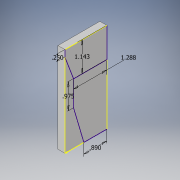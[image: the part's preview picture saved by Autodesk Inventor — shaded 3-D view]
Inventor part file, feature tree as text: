
AUTODESK INVENTOR PART (.ipt)
format: ipt  version: 2018 (Build 220112000, 112)  size: 104,448 bytes
history: native  units: in
note: dims shown in document units (in); Inventor stores cm internally (conversion verified against a paired STEP export)
features: sketch x2, extrude x1
ambient origin geometry x8: Origin, YZ Plane, XZ Plane, XY Plane, X Axis, Y Axis, Z Axis, Center Point
bodies: Solid1 (feature_tree)
feature tree (3):
  extrude  "Extrusion1"  Depth=1.622in
  sketch  "Sketch2"  dims[d2=3.472in d3=0.0in d4=1.143in d5=1.288in d6=0.975in d7=0.89in d8=0.25in]
  sketch  "Sketch1"  dims[d0=0.265in d1=1.622in]
